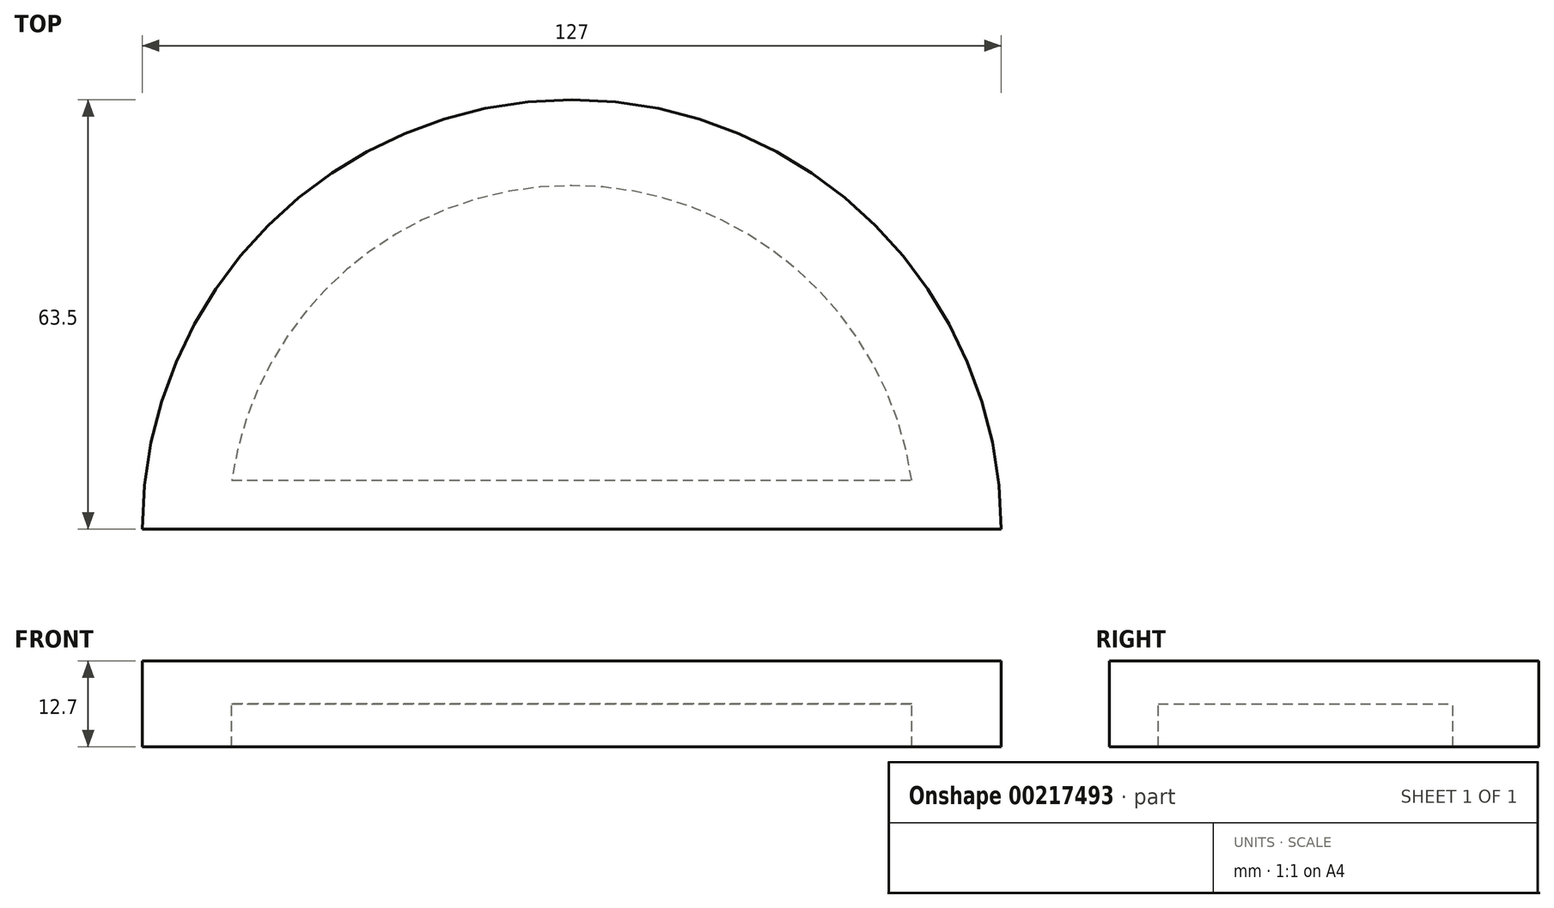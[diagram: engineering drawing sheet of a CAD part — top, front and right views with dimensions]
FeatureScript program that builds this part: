
annotation { "Feature Type Name" : "Feature", "Feature Type Description" : "" }
export const myFeature = defineFeature(function(context is Context, id is Id, definition is map)
    precondition{}
    {
        {
            var Q0;
            Q0=qCreatedBy(makeId("Top.planeOp"),FACE);
            var sketch = newSketch(context, id + "F0", { "sketchPlane" : qUnion([Q0])});
            skArc(sketch, "E0", {"start": v(63.5, 0) * mm, "mid": v(0, 63.5) * mm, "end": v(-63.5, 0) * mm});
            skLineSegment(sketch, "E1", {"start": v(-63.5, 0) * mm, "end": v(63.5, 0) * mm});
            skSolve(sketch);
        }
        {
            var Q0;
            Q0=qSketchRegion(id+"F0",true);
            extrude(context, id + "F1", {"entities" : qUnion([Q0]), "endBound" : BoundingType.SYMMETRIC, "depth" : 12.7 * mm});
        }
        {
            var Q0;
            Q0=qCreatedBy(makeId("Top.planeOp"),FACE);
            var sketch = newSketch(context, id + "F2", { "sketchPlane" : qUnion([Q0])});
            skArc(sketch, "E2", {"start": v(50.28, 7.22) * mm, "mid": v(0, 50.8) * mm, "end": v(-50.28, 7.22) * mm});
            skLineSegment(sketch, "E3", {"start": v(-50.28, 7.22) * mm, "end": v(50.28, 7.22) * mm});
            skSolve(sketch);
        }
        {
            var Q0;
            Q0=qSketchRegion(id+"F2",true);
            extrude(context, id + "F3", {"entities" : qUnion([Q0]), "operationType" : NewBodyOperationType.REMOVE, "oppositeDirection" : true, "depth" : 25.4 * mm});
        }
    });
